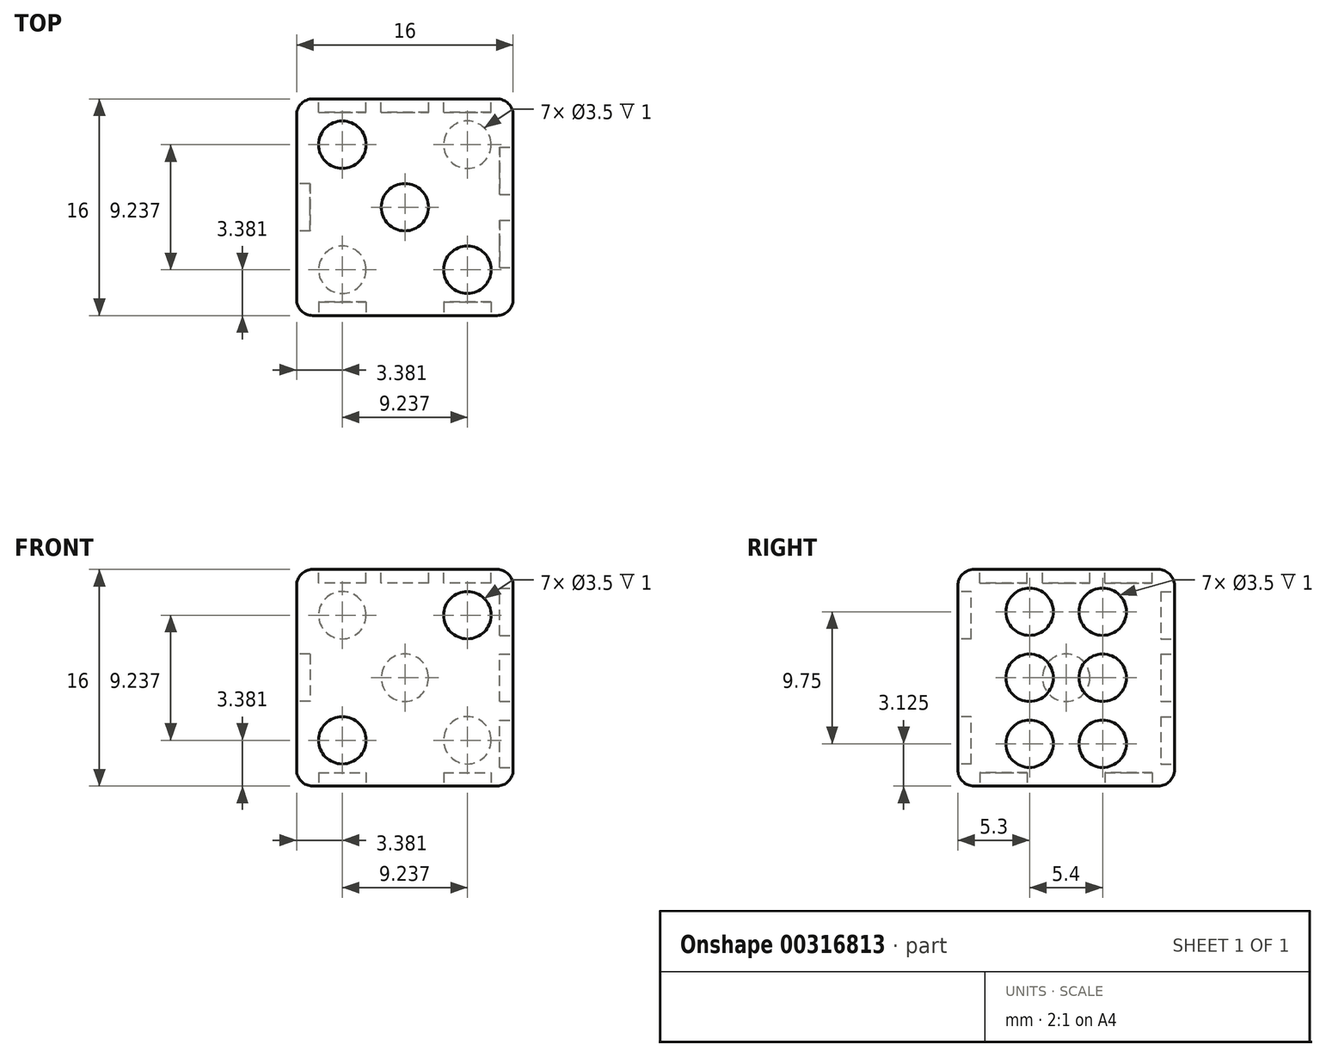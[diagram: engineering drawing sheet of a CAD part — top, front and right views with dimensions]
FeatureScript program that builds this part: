
annotation { "Feature Type Name" : "Feature", "Feature Type Description" : "" }
export const myFeature = defineFeature(function(context is Context, id is Id, definition is map)
    precondition{}
    {
        {
            var Q0;
            Q0=qCreatedBy(makeId("Top.planeOp"),FACE);
            var sketch = newSketch(context, id + "F0", { "sketchPlane" : qUnion([Q0])});
            skLineSegment(sketch, "E0.bottom", {"start": v(8, 8) * mm, "end": v(-8, 8) * mm});
            skLineSegment(sketch, "E0.top", {"start": v(8, -8) * mm, "end": v(-8, -8) * mm});
            skLineSegment(sketch, "E0.left", {"start": v(8, 8) * mm, "end": v(8, -8) * mm});
            skLineSegment(sketch, "E0.right", {"start": v(-8, 8) * mm, "end": v(-8, -8) * mm});
            skPoint(sketch, "E0.middle", {"position": v(0, 0) * mm});
            skSolve(sketch);
        }
        {
            var Q0;
            Q0 = qSketchRegion(id + "F0", true);
            extrude(context, id + "F1", {"entities" : qUnion([Q0]), "depth" : 16 * mm});
        }
        {
            var Q0;
            Q0=makeQuery(id+"F1.opExtrude","CAP_FACE",FACE,{"disambiguationData":[OSD([sQuery(id+"F0.wireOp",EDGE,"E0.bottom"),sQuery(id+"F0.wireOp",EDGE,"E0.top"),sQuery(id+"F0.wireOp",EDGE,"E0.left"),sQuery(id+"F0.wireOp",EDGE,"E0.right")])],"isStart":false});
            var sketch = newSketch(context, id + "F2", { "sketchPlane" : qUnion([Q0])});
            skCircle(sketch, "E1", {"center": v(0, 0) * mm, "radius": 1.75 * mm});
            skPoint(sketch, "E2", {"position": v(1.24, 1.24) * mm});
            skPoint(sketch, "E3", {"position": v(-1.24, -1.24) * mm});
            skCircle(sketch, "E4", {"center": v(-4.62, 4.62) * mm, "radius": 1.75 * mm});
            skCircle(sketch, "E5", {"center": v(4.62, -4.62) * mm, "radius": 1.75 * mm});
            skPoint(sketch, "E6", {"position": v(-3.38, -3.38) * mm});
            skPoint(sketch, "E7", {"position": v(-5.86, -5.86) * mm});
            skSolve(sketch);
        }
        {
            var Q0;
            Q0=makeQuery(id+"F2.imprint","IMPRINT",FACE,{"disambiguationData":[TD([[makeQuery(id+"F2.imprint","IMPRINT",EDGE,{"derivedFrom":sQuery(id+"F2.wireOp",EDGE,"E4")}),1.0]])]});
            var Q1;
            Q1=makeQuery(id+"F2.imprint","IMPRINT",FACE,{"disambiguationData":[TD([[makeQuery(id+"F2.imprint","IMPRINT",EDGE,{"derivedFrom":sQuery(id+"F2.wireOp",EDGE,"E5")}),1.0]])]});
            var Q2;
            Q2=makeQuery(id+"F2.imprint","IMPRINT",FACE,{"disambiguationData":[TD([[makeQuery(id+"F2.imprint","IMPRINT",EDGE,{"derivedFrom":sQuery(id+"F2.wireOp",EDGE,"E1")}),1.0]])]});
            extrude(context, id + "F3", {"entities" : qUnion([Q0, Q1, Q2]), "operationType" : NewBodyOperationType.REMOVE, "oppositeDirection" : true, "depth" : 1 * mm});
        }
        {
            var Q0;
            Q0=makeQuery(id+"F1.opExtrude","SWEPT_FACE",FACE,{"disambiguationData":[OSD([sQuery(id+"F0.wireOp",EDGE,"E0.top")])]});
            var sketch = newSketch(context, id + "F4", { "sketchPlane" : qUnion([Q0])});
            skPoint(sketch, "E8", {"position": v(-4.62, 3.38) * mm});
            skCircle(sketch, "E9", {"center": v(-4.62, 3.38) * mm, "radius": 1.75 * mm});
            skCircle(sketch, "E10", {"center": v(4.62, 12.62) * mm, "radius": 1.75 * mm});
            skSolve(sketch);
        }
        {
            var Q0;
            Q0=makeQuery(id+"F4.imprint","IMPRINT",FACE,{"disambiguationData":[TD([[makeQuery(id+"F4.imprint","IMPRINT",EDGE,{"derivedFrom":sQuery(id+"F4.wireOp",EDGE,"E9")}),1.0]])]});
            var Q1;
            Q1=makeQuery(id+"F4.imprint","IMPRINT",FACE,{"disambiguationData":[TD([[makeQuery(id+"F4.imprint","IMPRINT",EDGE,{"derivedFrom":sQuery(id+"F4.wireOp",EDGE,"E10")}),1.0]])]});
            extrude(context, id + "F5", {"entities" : qUnion([Q0, Q1]), "operationType" : NewBodyOperationType.REMOVE, "oppositeDirection" : true, "depth" : 1 * mm});
        }
        {
            var Q0;
            Q0=makeQuery(id+"F1.opExtrude","SWEPT_FACE",FACE,{"disambiguationData":[OSD([sQuery(id+"F0.wireOp",EDGE,"E0.right")])]});
            var sketch = newSketch(context, id + "F6", { "sketchPlane" : qUnion([Q0])});
            skCircle(sketch, "E11", {"center": v(0, 8) * mm, "radius": 1.75 * mm});
            skPoint(sketch, "E11.centerSnap0", {"position": v(-8, 8) * mm});
            skPoint(sketch, "E11.centerSnap1", {"position": v(0, 16) * mm});
            skSolve(sketch);
        }
        {
            var Q0;
            Q0 = qSketchRegion(id + "F6", true);
            extrude(context, id + "F7", {"entities" : qUnion([Q0]), "operationType" : NewBodyOperationType.REMOVE, "oppositeDirection" : true, "depth" : 1 * mm});
        }
        {
            var Q0;
            Q0=makeQuery(id+"F1.opExtrude","SWEPT_FACE",FACE,{"disambiguationData":[OSD([sQuery(id+"F0.wireOp",EDGE,"E0.left")])]});
            var sketch = newSketch(context, id + "F8", { "sketchPlane" : qUnion([Q0])});
            skPoint(sketch, "E12", {"position": v(-2.7, 16) * mm});
            skPoint(sketch, "E13", {"position": v(2.7, 16) * mm});
            skPoint(sketch, "E14", {"position": v(-2.7, 8) * mm});
            skPoint(sketch, "E15", {"position": v(2.7, 8) * mm});
            skCircle(sketch, "E16", {"center": v(-2.7, 8) * mm, "radius": 1.75 * mm});
            skCircle(sketch, "E17", {"center": v(2.7, 8) * mm, "radius": 1.75 * mm});
            skPoint(sketch, "E18", {"position": v(-2.7, 9.75) * mm});
            skPoint(sketch, "E19", {"position": v(2.7, 9.75) * mm});
            skPoint(sketch, "E20", {"position": v(2.7, 6.25) * mm});
            skPoint(sketch, "E21", {"position": v(-2.7, 6.25) * mm});
            skCircle(sketch, "E22", {"center": v(-2.7, 12.88) * mm, "radius": 1.75 * mm});
            skCircle(sketch, "E23", {"center": v(2.7, 12.88) * mm, "radius": 1.75 * mm});
            skCircle(sketch, "E24", {"center": v(2.7, 3.12) * mm, "radius": 1.75 * mm});
            skCircle(sketch, "E25", {"center": v(-2.7, 3.12) * mm, "radius": 1.75 * mm});
            skSolve(sketch);
        }
        {
            var Q0;
            Q0=makeQuery(id+"F8.imprint","IMPRINT",FACE,{"disambiguationData":[TD([[makeQuery(id+"F8.imprint","IMPRINT",EDGE,{"derivedFrom":sQuery(id+"F8.wireOp",EDGE,"E16")}),1.0]])]});
            var Q1;
            Q1=makeQuery(id+"F8.imprint","IMPRINT",FACE,{"disambiguationData":[TD([[makeQuery(id+"F8.imprint","IMPRINT",EDGE,{"derivedFrom":sQuery(id+"F8.wireOp",EDGE,"E17")}),1.0]])]});
            var Q2;
            Q2=makeQuery(id+"F8.imprint","IMPRINT",FACE,{"disambiguationData":[TD([[makeQuery(id+"F8.imprint","IMPRINT",EDGE,{"derivedFrom":sQuery(id+"F8.wireOp",EDGE,"E23")}),1.0]])]});
            var Q3;
            Q3=makeQuery(id+"F8.imprint","IMPRINT",FACE,{"disambiguationData":[TD([[makeQuery(id+"F8.imprint","IMPRINT",EDGE,{"derivedFrom":sQuery(id+"F8.wireOp",EDGE,"E24")}),1.0]])]});
            var Q4;
            Q4=makeQuery(id+"F8.imprint","IMPRINT",FACE,{"disambiguationData":[TD([[makeQuery(id+"F8.imprint","IMPRINT",EDGE,{"derivedFrom":sQuery(id+"F8.wireOp",EDGE,"E25")}),1.0]])]});
            var Q5;
            Q5=makeQuery(id+"F8.imprint","IMPRINT",FACE,{"disambiguationData":[TD([[makeQuery(id+"F8.imprint","IMPRINT",EDGE,{"derivedFrom":sQuery(id+"F8.wireOp",EDGE,"E22")}),1.0]])]});
            extrude(context, id + "F9", {"entities" : qUnion([Q0, Q1, Q2, Q3, Q4, Q5]), "operationType" : NewBodyOperationType.REMOVE, "oppositeDirection" : true, "depth" : 1 * mm});
        }
        {
            var Q0;
            Q0=makeQuery(id+"F1.opExtrude","SWEPT_FACE",FACE,{"disambiguationData":[OSD([sQuery(id+"F0.wireOp",EDGE,"E0.bottom")])]});
            var sketch = newSketch(context, id + "F10", { "sketchPlane" : qUnion([Q0])});
            skLineSegment(sketch, "E26", {"start": v(8, 0) * mm, "end": v(8, 16) * mm});
            skCircle(sketch, "E27", {"center": v(0, 8) * mm, "radius": 1.75 * mm});
            skPoint(sketch, "E28", {"position": v(-1.24, 9.24) * mm});
            skPoint(sketch, "E29", {"position": v(1.24, 9.24) * mm});
            skPoint(sketch, "E30", {"position": v(1.24, 6.76) * mm});
            skPoint(sketch, "E31", {"position": v(-1.24, 6.76) * mm});
            skCircle(sketch, "E32", {"center": v(-4.62, 3.38) * mm, "radius": 1.75 * mm});
            skCircle(sketch, "E33", {"center": v(-4.62, 12.62) * mm, "radius": 1.75 * mm});
            skCircle(sketch, "E34", {"center": v(4.62, 12.62) * mm, "radius": 1.75 * mm});
            skCircle(sketch, "E35", {"center": v(4.62, 3.38) * mm, "radius": 1.75 * mm});
            skSolve(sketch);
        }
        {
            var Q0;
            Q0 = qSketchRegion(id + "F10", true);
            extrude(context, id + "F11", {"entities" : qUnion([Q0]), "operationType" : NewBodyOperationType.REMOVE, "oppositeDirection" : true, "depth" : 1 * mm});
        }
        {
            var Q0;
            Q0=makeQuery(id+"F1.opExtrude","CAP_FACE",FACE,{"disambiguationData":[OSD([sQuery(id+"F0.wireOp",EDGE,"E0.bottom"),sQuery(id+"F0.wireOp",EDGE,"E0.top"),sQuery(id+"F0.wireOp",EDGE,"E0.left"),sQuery(id+"F0.wireOp",EDGE,"E0.right")])],"isStart":true});
            var sketch = newSketch(context, id + "F12", { "sketchPlane" : qUnion([Q0])});
            skLineSegment(sketch, "E36", {"start": v(-8, 8) * mm, "end": v(-8, -8) * mm});
            skPoint(sketch, "E37", {"position": v(1.24, -1.24) * mm});
            skPoint(sketch, "E38", {"position": v(-1.24, -1.24) * mm});
            skPoint(sketch, "E39", {"position": v(-1.24, 1.24) * mm});
            skPoint(sketch, "E40", {"position": v(1.24, 1.24) * mm});
            skCircle(sketch, "E41", {"center": v(4.62, -4.62) * mm, "radius": 1.75 * mm});
            skCircle(sketch, "E42", {"center": v(-4.62, -4.62) * mm, "radius": 1.75 * mm});
            skCircle(sketch, "E43", {"center": v(-4.62, 4.62) * mm, "radius": 1.75 * mm});
            skCircle(sketch, "E44", {"center": v(4.62, 4.62) * mm, "radius": 1.75 * mm});
            skSolve(sketch);
        }
        {
            var Q0;
            Q0 = qSketchRegion(id + "F12", true);
            extrude(context, id + "F13", {"entities" : qUnion([Q0]), "operationType" : NewBodyOperationType.REMOVE, "oppositeDirection" : true, "depth" : 1 * mm});
        }
        {
            var Q0;
            Q0=makeQuery(id+"F1.opExtrude","CAP_EDGE",EDGE,{"disambiguationData":[OSD([sQuery(id+"F0.wireOp",EDGE,"E0.bottom")])],"isStart":false});
            var Q1;
            Q1=makeQuery(id+"F1.opExtrude","CAP_EDGE",EDGE,{"disambiguationData":[OSD([sQuery(id+"F0.wireOp",EDGE,"E0.right")])],"isStart":false});
            var Q2;
            Q2=makeQuery(id+"F1.opExtrude","SWEPT_EDGE",EDGE,{"disambiguationData":[OSD([sQuery(id+"F0.wireOp",EDGE,"E0.bottom"),sQuery(id+"F0.wireOp",EDGE,"E0.right")])]});
            var Q3;
            Q3=makeQuery(id+"F1.opExtrude","SWEPT_EDGE",EDGE,{"disambiguationData":[OSD([sQuery(id+"F0.wireOp",EDGE,"E0.top"),sQuery(id+"F0.wireOp",EDGE,"E0.right")])]});
            var Q4;
            Q4=makeQuery(id+"F1.opExtrude","CAP_EDGE",EDGE,{"disambiguationData":[OSD([sQuery(id+"F0.wireOp",EDGE,"E0.top")])],"isStart":false});
            var Q5;
            Q5=makeQuery(id+"F1.opExtrude","SWEPT_EDGE",EDGE,{"disambiguationData":[OSD([sQuery(id+"F0.wireOp",EDGE,"E0.top"),sQuery(id+"F0.wireOp",EDGE,"E0.left")])]});
            var Q6;
            Q6=makeQuery(id+"F1.opExtrude","CAP_EDGE",EDGE,{"disambiguationData":[OSD([sQuery(id+"F0.wireOp",EDGE,"E0.left")])],"isStart":true});
            var Q7;
            Q7=makeQuery(id+"F1.opExtrude","SWEPT_EDGE",EDGE,{"disambiguationData":[OSD([sQuery(id+"F0.wireOp",EDGE,"E0.bottom"),sQuery(id+"F0.wireOp",EDGE,"E0.left")])]});
            var Q8;
            Q8=makeQuery(id+"F1.opExtrude","CAP_EDGE",EDGE,{"disambiguationData":[OSD([sQuery(id+"F0.wireOp",EDGE,"E0.bottom")])],"isStart":true});
            var Q9;
            Q9=makeQuery(id+"F1.opExtrude","CAP_EDGE",EDGE,{"disambiguationData":[OSD([sQuery(id+"F0.wireOp",EDGE,"E0.right")])],"isStart":true});
            var Q10;
            Q10=makeQuery(id+"F1.opExtrude","CAP_EDGE",EDGE,{"disambiguationData":[OSD([sQuery(id+"F0.wireOp",EDGE,"E0.top")])],"isStart":true});
            var Q11;
            Q11=makeQuery(id+"F1.opExtrude","CAP_EDGE",EDGE,{"disambiguationData":[OSD([sQuery(id+"F0.wireOp",EDGE,"E0.left")])],"isStart":false});
            fillet(context, id + "F14", {"entities" : qUnion([Q0, Q1, Q2, Q3, Q4, Q5, Q6, Q7, Q8, Q9, Q10, Q11]), "radius" : 1.2 * mm, "tangentPropagation" : true, "allowEdgeOverflow" : false});
        }
    });
